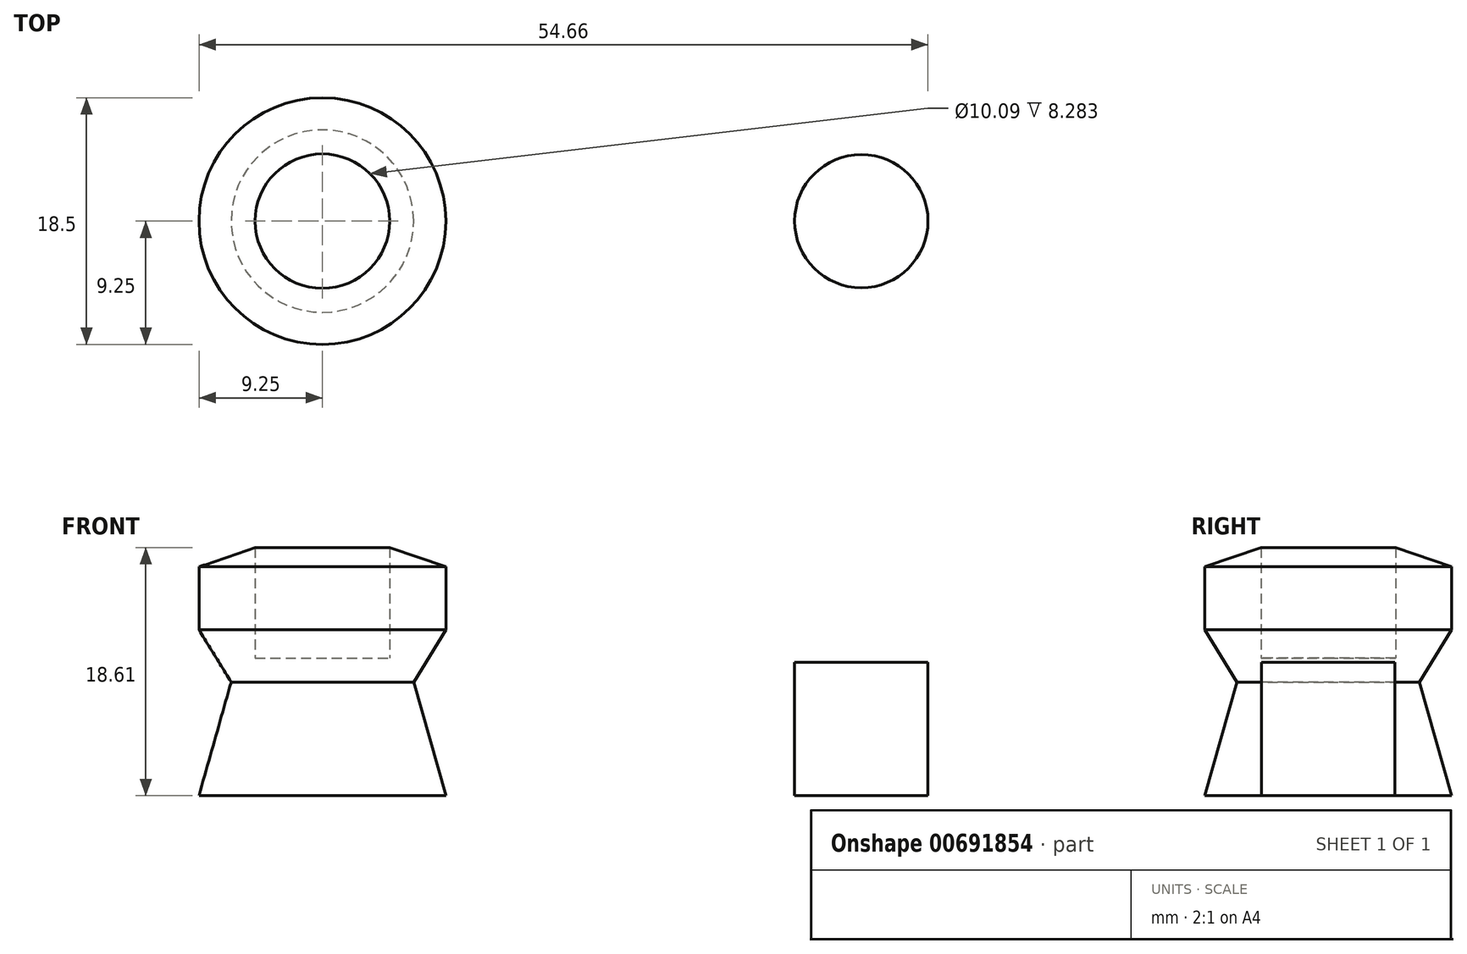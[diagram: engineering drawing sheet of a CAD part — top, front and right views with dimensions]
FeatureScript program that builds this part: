
annotation { "Feature Type Name" : "Feature", "Feature Type Description" : "" }
export const myFeature = defineFeature(function(context is Context, id is Id, definition is map)
    precondition{}
    {
        {
            var Q0;
            Q0=qCreatedBy(makeId("Front.planeOp"),FACE);
            var sketch = newSketch(context, id + "F0", { "sketchPlane" : qUnion([Q0])});
            skLineSegment(sketch, "E0", {"start": v(0, 0) * mm, "end": v(0, 20.33) * mm});
            skLineSegment(sketch, "E1", {"start": v(0, 0) * mm, "end": v(9.25, 0) * mm});
            skLineSegment(sketch, "E2", {"start": v(9.25, 0) * mm, "end": v(6.4, 10.12) * mm});
            skLineSegment(sketch, "E3", {"start": v(8.85, 17.3) * mm, "end": v(0, 20.33) * mm});
            skLineSegment(sketch, "E4", {"start": v(0, 11.27) * mm, "end": v(5.04, 11.27) * mm});
            skLineSegment(sketch, "E5", {"start": v(5.04, 11.27) * mm, "end": v(5.04, 20.33) * mm});
            skLineSegment(sketch, "E6", {"start": v(5.04, 20.33) * mm, "end": v(0, 20.33) * mm});
            skLineSegment(sketch, "E7", {"start": v(5.04, 11.27) * mm, "end": v(5.04, 10.32) * mm});
            skLineSegment(sketch, "E8", {"start": v(5.04, 10.32) * mm, "end": v(0, 10.32) * mm});
            skLineSegment(sketch, "E9", {"start": v(45.41, 0) * mm, "end": v(45.41, 10) * mm});
            skLineSegment(sketch, "E10", {"start": v(45.41, 10) * mm, "end": v(40.41, 10) * mm});
            skLineSegment(sketch, "E11", {"start": v(40.41, 10) * mm, "end": v(40.41, 0) * mm});
            skLineSegment(sketch, "E12", {"start": v(40.41, 0) * mm, "end": v(45.41, 0) * mm});
            skLineSegment(sketch, "E13", {"start": v(8.85, 17.3) * mm, "end": v(9.25, 17.17) * mm});
            skLineSegment(sketch, "E14", {"start": v(9.25, 14.09) * mm, "end": v(9.25, 17.17) * mm});
            skLineSegment(sketch, "E15", {"start": v(9.25, 14.09) * mm, "end": v(9.25, 12.44) * mm});
            skLineSegment(sketch, "E16", {"start": v(9.25, 12.44) * mm, "end": v(6.84, 8.52) * mm});
            skSolve(sketch);
        }
        {
            var Q0;
            {var subQ1=sQuery(id+"F0.wireOp",EDGE,"E1");Q0=makeQuery(id+"F0.imprint","IMPRINT",FACE,{"disambiguationData":[TD([[makeQuery(id+"F0.imprint","IMPRINT",EDGE,{"derivedFrom":subQ1}),1.0]])]});}
            var Q1;
            Q1=makeQuery(id+"F0.imprint","IMPRINT",FACE,{"disambiguationData":[TD([[makeQuery(id+"F0.imprint","IMPRINT",EDGE,{"derivedFrom":sQuery(id+"F0.wireOp",EDGE,"wnLaPhQU-ftcD-Gic3-7AHv-snN9PaO8BY6I")}),1.0]])]});
            var Q2;
            Q2=sQuery(id+"F0.wireOp",EDGE,"E0");
            revolve(context, id + "F1", {"entities" : qUnion([Q0, Q1]), "axis" : qUnion([Q2]), "revolveType" : RevolveType.FULL});
        }
        {
            var Q0;
            Q0=makeQuery(id+"F0.imprint","IMPRINT",FACE,{"disambiguationData":[TD([[makeQuery(id+"F0.imprint","IMPRINT",EDGE,{"derivedFrom":sQuery(id+"F0.wireOp",EDGE,"E9")}),1.0]])]});
            var Q1;
            Q1=sQuery(id+"F0.wireOp",EDGE,"E11");
            revolve(context, id + "F2", {"entities" : qUnion([Q0]), "axis" : qUnion([Q1]), "revolveType" : RevolveType.FULL});
        }
    });
